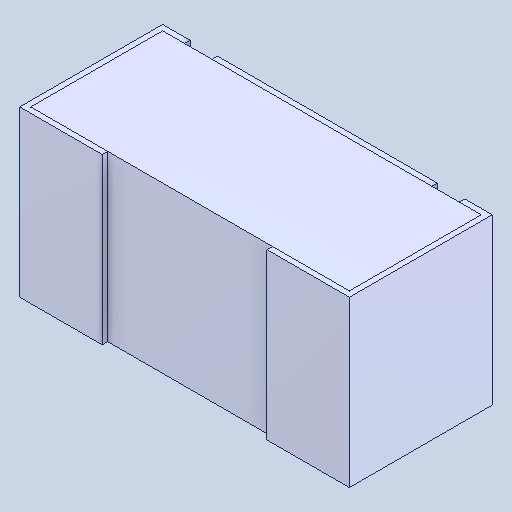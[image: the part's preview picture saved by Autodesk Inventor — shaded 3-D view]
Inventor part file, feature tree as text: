
AUTODESK INVENTOR PART (.ipt)
format: ipt  version: 2025 (Build 290162000, 162)  size: 110,592 bytes
history: native  units: mm
features: boolean_combine x2, other x1, mirror x1
ambient origin geometry x8: Origin, YZ Plane, XZ Plane, XY Plane, X Axis, Y Axis, Z Axis, Center Point
bodies: Solid1 (feature_tree), Solid2 (feature_tree), Solid3 (feature_tree), Solid4 (feature_tree)
feature tree (4):
  other  "Cut-Extrude1"
  boolean_combine  "Combine2"
  mirror  "Mirror1[3]"
  boolean_combine  "Combine1"
